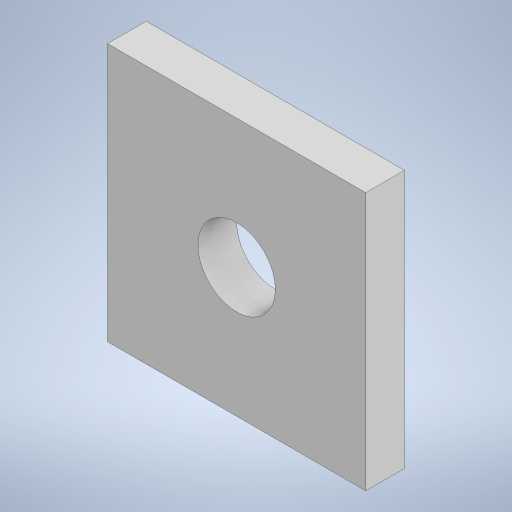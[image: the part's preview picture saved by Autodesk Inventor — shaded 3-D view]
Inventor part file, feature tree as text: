
AUTODESK INVENTOR PART (.ipt)
format: ipt  version: 2023 (Build 270158000, 158)  size: 216,576 bytes
history: native  units: mm
features: extrude x2, sketch x2
ambient origin geometry x8: Origin, YZ Plane, XZ Plane, XY Plane, X Axis, Y Axis, Z Axis, Center Point
bodies: Body1 (feature_tree)
feature tree (4):
  extrude  "Extrusion45"  Depth=20.0mm
  extrude  "Extrusion46"  Depth=3.0mm
  sketch  "Sketch66"  dims[d179=20.0mm d180=20.0mm]
  sketch  "Sketch67"  dims[d181=3.0mm d182=0.0mm d183=6.0mm d184=3.0mm d185=0.0mm d49=0.5mm d50=0.872665mm d51=0.5mm d52=0.872665mm d130=0.5mm d131=0.872665mm d132=0.5mm d133=0.872665mm d156=0.5mm d157=0.872665mm d158=0.5mm d159=0.872665mm]
